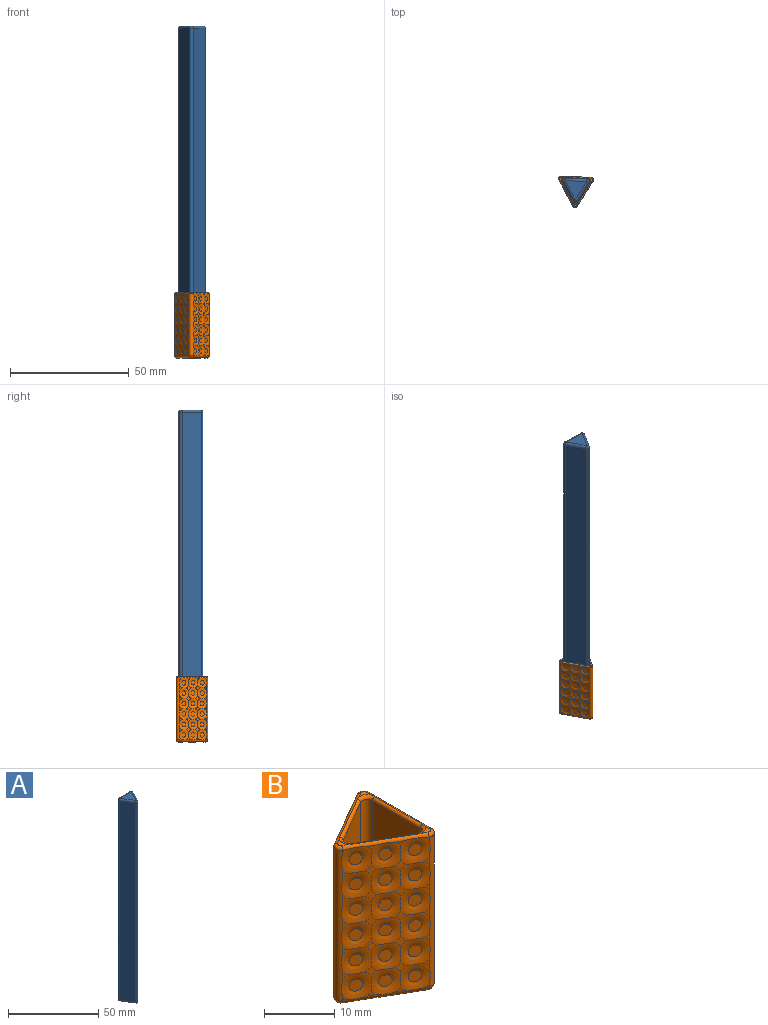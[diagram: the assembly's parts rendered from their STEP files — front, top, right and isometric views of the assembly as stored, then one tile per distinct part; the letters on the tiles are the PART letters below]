
ASSEMBLY  parts=2 mates=1
PART A: 20 faces, bbox 11.2x10.2x137.5 mm
  f0: plane 135.5x7.83mm, normal (-0.85,-0.53,0), area 1251.7mm2, adj f8,f13,f16,f19
  f1: plane 135.5x8.16mm, normal (0.88,-0.47,0), area 1251.7mm2, adj f6,f14,f15,f19
  f2: plane 135.5x9.23mm, normal (-0.04,1,0), area 1251.7mm2, adj f5,f6,f7,f8
  f3: plane 9.23x8.16mm, normal (0,0,1), area 37mm2, adj f5,f13,f14
  f4: plane 9.23x8.16mm, normal (0,0,-1), area 37mm2, adj f7,f15,f16
  f5: cylinder r=1mm len=9.27mm, axis (1,0.04,0), area 14.5mm2, adj f2,f3,f9,f10
  f6: cylinder r=1mm len=135.5mm, axis (0,0,-1), area 283.8mm2, adj f1,f2,f10,f11
  f7: cylinder r=1mm len=9.27mm, axis (-1,-0.04,0), area 14.5mm2, adj f2,f4,f11,f12
  f8: cylinder r=1mm len=135.5mm, axis (0,0,-1), area 283.8mm2, adj f0,f2,f9,f12
  f9: sphere r=1mm, area 2.1mm2, adj f5,f8,f13
  f10: sphere r=1mm, area 2.1mm2, adj f5,f6,f14
  f11: sphere r=1mm, area 2.1mm2, adj f6,f7,f15
  f12: sphere r=1mm, area 2.1mm2, adj f7,f8,f16
  f13: cylinder r=1mm len=8.36mm, axis (-0.53,0.85,0), area 14.5mm2, adj f0,f3,f9,f17
  f14: cylinder r=1mm len=8.63mm, axis (-0.47,-0.88,0), area 14.5mm2, adj f1,f3,f10,f17
  f15: cylinder r=1mm len=8.63mm, axis (0.47,0.88,0), area 14.5mm2, adj f1,f4,f11,f18
  f16: cylinder r=1mm len=8.36mm, axis (0.53,-0.85,0), area 14.5mm2, adj f0,f4,f12,f18
  f17: sphere r=1mm, area 2.1mm2, adj f13,f14,f19
  f18: sphere r=1mm, area 2.1mm2, adj f15,f16,f19
  f19: cylinder r=1mm len=135.5mm, axis (0,0,-1), area 283.8mm2, adj f0,f1,f17,f18
PART B: 243 faces, bbox 13.2x14.9x27.6 mm
  f0: plane 0.94x0.82mm, normal (0,0,-1), area 0.4mm2, adj f99,f105,f242
  f1: plane 0.94x0.82mm, normal (0,0,-1), area 0.4mm2, adj f99,f102,f240
  f2: plane 3.04x1.28mm, normal (0,0,-1), area 2.7mm2, adj f99,f240,f241,f242
  f3: plane 2.76x2.34mm, normal (0,0,-1), area 2.7mm2, adj f105,f239,f241,f242
  f4: plane 0.94x0.82mm, normal (0,0,-1), area 0.4mm2, adj f102,f105,f239
  f5: plane 0.4x0.35mm, normal (-0.5,-0.87,0), area 0.1mm2, adj f101,f102,f234
  f6: plane 0.4x0.35mm, normal (-0.5,-0.87,0), area 0.1mm2, adj f97,f102,f231
  f7: plane 1x0.65mm, normal (-0.5,-0.87,0), area 0.3mm2, adj f102,f231,f233
  f8: plane 1x0.65mm, normal (-0.5,-0.87,0), area 0.3mm2, adj f102,f233,f234
  f9: plane 1.2x0.6mm, normal (-0.5,-0.87,0), area 0.4mm2, adj f97,f228,f231
  f10: plane 1.7x1.5mm, normal (-0.5,-0.87,0), area 1.2mm2, adj f228,f230,f231,f233
  f11: plane 1.7x1.5mm, normal (-0.5,-0.87,0), area 1.2mm2, adj f230,f232,f233,f234
  f12: plane 1.2x0.6mm, normal (-0.5,-0.87,0), area 0.4mm2, adj f101,f232,f234
  f13: plane 1.7x1.5mm, normal (-0.5,-0.87,0), area 1.2mm2, adj f227,f229,f230,f232
  f14: plane 1.2x0.6mm, normal (-0.5,-0.87,0), area 0.4mm2, adj f101,f229,f232
  f15: plane 1.2x0.6mm, normal (-0.5,-0.87,0), area 0.4mm2, adj f97,f225,f228
  f16: plane 1.7x1.5mm, normal (-0.5,-0.87,0), area 1.2mm2, adj f225,f227,f228,f230
  f17: plane 1.2x0.6mm, normal (-0.5,-0.87,0), area 0.4mm2, adj f97,f222,f225
  f18: plane 1.7x1.5mm, normal (-0.5,-0.87,0), area 1.2mm2, adj f222,f224,f225,f227
  f19: plane 1.7x1.5mm, normal (-0.5,-0.87,0), area 1.2mm2, adj f224,f226,f227,f229
  f20: plane 1.2x0.6mm, normal (-0.5,-0.87,0), area 0.4mm2, adj f101,f226,f229
  f21: plane 1.2x0.6mm, normal (-0.5,-0.87,0), area 0.4mm2, adj f101,f223,f226
  f22: plane 1.7x1.5mm, normal (-0.5,-0.87,0), area 1.2mm2, adj f221,f223,f224,f226
  f23: plane 1.2x0.6mm, normal (-0.5,-0.87,0), area 0.4mm2, adj f97,f219,f222
  f24: plane 1.7x1.5mm, normal (-0.5,-0.87,0), area 1.2mm2, adj f219,f221,f222,f224
  f25: plane 0.4x0.35mm, normal (-0.5,-0.87,0), area 0.1mm2, adj f97,f123,f217
  f26: plane 1.2x0.6mm, normal (-0.5,-0.87,0), area 0.4mm2, adj f97,f217,f219
  f27: plane 1x0.65mm, normal (-0.5,-0.87,0), area 0.3mm2, adj f123,f217,f218
  f28: plane 1.7x1.5mm, normal (-0.5,-0.87,0), area 1.2mm2, adj f217,f218,f219,f221
  f29: plane 1.7x1.5mm, normal (-0.5,-0.87,0), area 1.2mm2, adj f218,f220,f221,f223
  f30: plane 1.2x0.6mm, normal (-0.5,-0.87,0), area 0.4mm2, adj f101,f220,f223
  f31: plane 0.4x0.35mm, normal (-0.5,-0.87,0), area 0.1mm2, adj f101,f123,f220
  f32: plane 0.69x0.6mm, normal (-0.5,0.87,0), area 0.2mm2, adj f101,f105,f198
  f33: plane 1.78x0.92mm, normal (-0.5,0.87,0), area 0.8mm2, adj f101,f197,f198
  f34: plane 1.78x0.92mm, normal (-0.5,0.87,0), area 0.8mm2, adj f101,f195,f197
  f35: plane 1.5x1.01mm, normal (-0.5,0.87,0), area 0.7mm2, adj f105,f196,f198
  f36: plane 2.41x2.14mm, normal (-0.5,0.87,0), area 2.2mm2, adj f194,f196,f197,f198
  f37: plane 1.5x1.01mm, normal (-0.5,0.87,0), area 0.7mm2, adj f105,f193,f196
  f38: plane 0.69x0.6mm, normal (-0.5,0.87,0), area 0.2mm2, adj f100,f105,f193
  f39: plane 2.41x2.14mm, normal (-0.5,0.87,0), area 2.2mm2, adj f190,f193,f194,f196
  f40: plane 1.78x0.92mm, normal (-0.5,0.87,0), area 0.8mm2, adj f100,f190,f193
  f41: plane 2.41x2.14mm, normal (-0.5,0.87,0), area 2.2mm2, adj f191,f194,f195,f197
  f42: plane 2.41x2.14mm, normal (-0.5,0.87,0), area 2.2mm2, adj f187,f190,f191,f194
  f43: plane 1.78x0.92mm, normal (-0.5,0.87,0), area 0.8mm2, adj f100,f187,f190
  f44: plane 1.78x0.92mm, normal (-0.5,0.87,0), area 0.8mm2, adj f101,f192,f195
  f45: plane 2.41x2.14mm, normal (-0.5,0.87,0), area 2.2mm2, adj f188,f191,f192,f195
  f46: plane 2.41x2.14mm, normal (-0.5,0.87,0), area 2.2mm2, adj f184,f187,f188,f191
  f47: plane 1.78x0.92mm, normal (-0.5,0.87,0), area 0.8mm2, adj f100,f184,f187
  f48: plane 1.78x0.92mm, normal (-0.5,0.87,0), area 0.8mm2, adj f101,f189,f192
  f49: plane 2.41x2.14mm, normal (-0.5,0.87,0), area 2.2mm2, adj f185,f188,f189,f192
  f50: plane 2.41x2.14mm, normal (-0.5,0.87,0), area 2.2mm2, adj f182,f184,f185,f188
  f51: plane 1.78x0.92mm, normal (-0.5,0.87,0), area 0.8mm2, adj f100,f182,f184
  f52: plane 0.69x0.6mm, normal (-0.5,0.87,0), area 0.2mm2, adj f101,f124,f186
  f53: plane 1.78x0.92mm, normal (-0.5,0.87,0), area 0.8mm2, adj f101,f186,f189
  f54: plane 1.5x1.01mm, normal (-0.5,0.87,0), area 0.7mm2, adj f124,f183,f186
  f55: plane 2.41x2.14mm, normal (-0.5,0.87,0), area 2.2mm2, adj f183,f185,f186,f189
  f56: plane 2.41x2.14mm, normal (-0.5,0.87,0), area 2.2mm2, adj f181,f182,f183,f185
  f57: plane 1.78x0.92mm, normal (-0.5,0.87,0), area 0.8mm2, adj f100,f181,f182
  f58: plane 0.69x0.6mm, normal (-0.5,0.87,0), area 0.2mm2, adj f100,f124,f181
  f59: plane 0.69x0.69mm, normal (1,0,0), area 0.2mm2, adj f97,f115,f162
  f60: plane 0.69x0.69mm, normal (1,0,0), area 0.2mm2, adj f100,f115,f158
  f61: plane 1.73x1.01mm, normal (1,0,0), area 0.7mm2, adj f115,f161,f162
  f62: plane 1.73x1.01mm, normal (1,0,0), area 0.7mm2, adj f115,f158,f161
  f63: plane 1.78x1.06mm, normal (1,0,0), area 0.8mm2, adj f100,f155,f158
  f64: plane 2.47x2.41mm, normal (1,0,0), area 2.2mm2, adj f155,f158,f159,f161
  f65: plane 1.78x1.06mm, normal (1,0,0), area 0.8mm2, adj f97,f160,f162
  f66: plane 2.47x2.41mm, normal (1,0,0), area 2.2mm2, adj f159,f160,f161,f162
  f67: plane 1.78x1.06mm, normal (1,0,0), area 0.8mm2, adj f97,f157,f160
  f68: plane 2.47x2.41mm, normal (1,0,0), area 2.2mm2, adj f156,f157,f159,f160
  f69: plane 2.47x2.41mm, normal (1,0,0), area 2.2mm2, adj f152,f155,f156,f159
  f70: plane 1.78x1.06mm, normal (1,0,0), area 0.8mm2, adj f100,f152,f155
  f71: plane 1.78x1.06mm, normal (1,0,0), area 0.8mm2, adj f100,f149,f152
  f72: plane 1.78x1.06mm, normal (1,0,0), area 0.8mm2, adj f100,f146,f149
  f73: plane 2.47x2.41mm, normal (1,0,0), area 2.2mm2, adj f149,f152,f153,f156
  f74: plane 2.47x2.41mm, normal (1,0,0), area 2.2mm2, adj f146,f149,f150,f153
  f75: plane 1.78x1.06mm, normal (1,0,0), area 0.8mm2, adj f97,f154,f157
  f76: plane 2.47x2.41mm, normal (1,0,0), area 2.2mm2, adj f153,f154,f156,f157
  f77: plane 1.78x1.06mm, normal (1,0,0), area 0.8mm2, adj f97,f151,f154
  f78: plane 2.47x2.41mm, normal (1,0,0), area 2.2mm2, adj f150,f151,f153,f154
  f79: plane 0.69x0.69mm, normal (1,0,0), area 0.2mm2, adj f97,f99,f148
  f80: plane 1.78x1.06mm, normal (1,0,0), area 0.8mm2, adj f97,f148,f151
  f81: plane 1.73x1.01mm, normal (1,0,0), area 0.7mm2, adj f99,f147,f148
  f82: plane 2.47x2.41mm, normal (1,0,0), area 2.2mm2, adj f147,f148,f150,f151
  f83: plane 2.47x2.41mm, normal (1,0,0), area 2.2mm2, adj f145,f146,f147,f150
  f84: plane 1.78x1.06mm, normal (1,0,0), area 0.8mm2, adj f100,f145,f146
  f85: plane 0.69x0.69mm, normal (1,0,0), area 0.2mm2, adj f99,f100,f145
  f86: plane 1.89x1.13mm, normal (0,0,1), area 0.9mm2, adj f119,f123,f124,f126
  f87: plane 1.63x1.52mm, normal (0,0,1), area 0.9mm2, adj f115,f117,f118,f123
  f88: plane 1x0.65mm, normal (-0.5,-0.87,0), area 0.3mm2, adj f123,f218,f220
  f89: plane 1.73x1.01mm, normal (1,0,0), area 0.7mm2, adj f99,f145,f147
  f90: plane 23.5x9.58mm, normal (-1,0,0), area 225.2mm2, adj f108,f112,f114,f116
  f91: plane 23.5x8.3mm, normal (0.5,0.87,0), area 225.2mm2, adj f106,f111,f114,f122
  f92: plane 23.5x8.3mm, normal (0.5,-0.87,0), area 225.2mm2, adj f106,f107,f108,f125
  f93: plane 1.5x1.01mm, normal (-0.5,0.87,0), area 0.7mm2, adj f124,f181,f183
  f94: plane 1.63x1.52mm, normal (0,0,1), area 0.9mm2, adj f115,f120,f121,f124
  f95: plane 9.58x8.3mm, normal (0,0,1), area 39.8mm2, adj f107,f111,f112
  f96: plane 2.76x2.34mm, normal (0,0,-1), area 2.7mm2, adj f102,f239,f240,f241
  f97: cylinder r=1mm len=26mm, axis (0,0,-1), area 50.9mm2, adj f6,f9,f15,f17,f23,f25,f26,f59
  f98: sphere r=1mm, area 2.1mm2, adj f97,f99,f102
  f99: cylinder r=1mm len=12.7mm, axis (0,-1,0), area 17.9mm2, adj f0,f1,f2,f79,f81,f85,f89,f98
  f100: cylinder r=1mm len=26mm, axis (0,0,-1), area 51.7mm2, adj f38,f40,f43,f47,f51,f57,f58,f60
  f101: cylinder r=1mm len=26mm, axis (0,0,-1), area 50.9mm2, adj f5,f12,f14,f20,f21,f30,f31,f32
  f102: cylinder r=1mm len=11.5mm, axis (-0.87,0.5,0), area 17.4mm2, adj f1,f4,f5,f6,f7,f8,f96,f98
  f103: sphere r=1mm, area 2.1mm2, adj f99,f100,f105
  f104: sphere r=1mm, area 2.1mm2, adj f101,f102,f105
  f105: cylinder r=1mm len=11.5mm, axis (0.87,0.5,0), area 17.9mm2, adj f0,f3,f4,f32,f35,f37,f38,f103
  f106: cylinder r=1mm len=23.5mm, axis (0,0,1), area 49.2mm2, adj f91,f92,f109,f126
  f107: cylinder r=1mm len=8.8mm, axis (-0.87,-0.5,0), area 15.1mm2, adj f92,f95,f109,f110
  f108: cylinder r=1mm len=23.5mm, axis (0,0,1), area 49.2mm2, adj f90,f92,f110,f121
  f109: sphere r=1mm, area 2.1mm2, adj f106,f107,f111
  f110: sphere r=1mm, area 2.1mm2, adj f107,f108,f112
  f111: cylinder r=1mm len=8.8mm, axis (0.87,-0.5,0), area 15.1mm2, adj f91,f95,f109,f113
  f112: cylinder r=1mm len=9.58mm, axis (0,1,0), area 15.1mm2, adj f90,f95,f110,f113
  f113: sphere r=1mm, area 2.1mm2, adj f111,f112,f114
  f114: cylinder r=1mm len=23.5mm, axis (0,0,1), area 49.2mm2, adj f90,f91,f113,f117
  f115: cylinder r=0.5mm len=12.7mm, axis (0,-1,0), area 8.9mm2, adj f59,f60,f61,f62,f87,f94,f116,f117
  f116: cylinder r=0.5mm len=9.58mm, axis (0,1,0), area 7mm2, adj f90,f115,f117,f121
  f117: torus R=1.5mm, axis (0,0,1), area 1.9mm2, adj f87,f114,f115,f116,f122,f123
  f118: torus R=0.5mm, axis (0,0,1), area 1.3mm2, adj f87,f97,f115,f123
  f119: torus R=0.5mm, axis (0,0,1), area 1.3mm2, adj f86,f101,f123,f124
  f120: torus R=0.5mm, axis (0,0,1), area 1.3mm2, adj f94,f100,f115,f124
  f121: torus R=1.5mm, axis (0,0,1), area 1.9mm2, adj f94,f108,f115,f116,f124,f125
  f122: cylinder r=0.5mm len=8.53mm, axis (0.87,-0.5,0), area 7mm2, adj f91,f117,f123,f126
  f123: cylinder r=0.5mm len=11.25mm, axis (-0.87,0.5,0), area 8.6mm2, adj f25,f27,f31,f86,f87,f88,f117,f118
  f124: cylinder r=0.5mm len=11.25mm, axis (0.87,0.5,0), area 8.9mm2, adj f52,f54,f58,f86,f93,f94,f119,f120
  f125: cylinder r=0.5mm len=8.53mm, axis (-0.87,-0.5,0), area 7mm2, adj f92,f121,f124,f126
  f126: torus R=1.5mm, axis (0,0,1), area 1.9mm2, adj f86,f106,f122,f123,f124,f125
  f127: plane 2x2mm, normal (1,0,0), area 3.1mm2, adj f145
  f128: plane 2x2mm, normal (1,0,0), area 3.1mm2, adj f158
  f129: plane 2x2mm, normal (1,0,0), area 3.1mm2, adj f157
  f130: plane 2x2mm, normal (1,0,0), area 3.1mm2, adj f156
  f131: plane 2x2mm, normal (1,0,0), area 3.1mm2, adj f152
  f132: plane 2x2mm, normal (1,0,0), area 3.1mm2, adj f155
  f133: plane 2x2mm, normal (1,0,0), area 3.1mm2, adj f159
  f134: plane 2x2mm, normal (1,0,0), area 3.1mm2, adj f160
  f135: plane 2x2mm, normal (1,0,0), area 3.1mm2, adj f162
  f136: plane 2x2mm, normal (1,0,0), area 3.1mm2, adj f161
  f137: plane 2x2mm, normal (1,0,0), area 3.1mm2, adj f147
  f138: plane 2x2mm, normal (1,0,0), area 3.1mm2, adj f148
  f139: plane 2x2mm, normal (1,0,0), area 3.1mm2, adj f151
  f140: plane 2x2mm, normal (1,0,0), area 3.1mm2, adj f150
  f141: plane 2x2mm, normal (1,0,0), area 3.1mm2, adj f146
  f142: plane 2x2mm, normal (1,0,0), area 3.1mm2, adj f149
  f143: plane 2x2mm, normal (1,0,0), area 3.1mm2, adj f153
  f144: plane 2x2mm, normal (1,0,0), area 3.1mm2, adj f154
  f145: torus R=2.39mm, axis (-1,0,0), area 14.1mm2, adj f83,f84,f85,f89,f99,f100,f127,f146
  f146: torus R=2.39mm, axis (-1,0,0), area 14.6mm2, adj f72,f74,f83,f84,f100,f141,f145,f149
  f147: torus R=2.39mm, axis (-1,0,0), area 14.6mm2, adj f81,f82,f83,f89,f99,f137,f145,f148
  f148: torus R=2.39mm, axis (-1,0,0), area 14.1mm2, adj f79,f80,f81,f82,f97,f99,f138,f147
  f149: torus R=2.39mm, axis (-1,0,0), area 14.6mm2, adj f71,f72,f73,f74,f100,f142,f146,f152
  f150: torus R=2.39mm, axis (-1,0,0), area 15.1mm2, adj f74,f78,f82,f83,f140,f146,f147,f151
  f151: torus R=2.39mm, axis (-1,0,0), area 14.6mm2, adj f77,f78,f80,f82,f97,f139,f148,f150
  f152: torus R=2.39mm, axis (-1,0,0), area 14.6mm2, adj f69,f70,f71,f73,f100,f131,f149,f155
  f153: torus R=2.39mm, axis (-1,0,0), area 15.1mm2, adj f73,f74,f76,f78,f143,f149,f150,f154
  f154: torus R=2.39mm, axis (-1,0,0), area 14.6mm2, adj f75,f76,f77,f78,f97,f144,f151,f153
  f155: torus R=2.39mm, axis (-1,0,0), area 14.6mm2, adj f63,f64,f69,f70,f100,f132,f152,f158
  f156: torus R=2.39mm, axis (-1,0,0), area 15.1mm2, adj f68,f69,f73,f76,f130,f152,f153,f157
  f157: torus R=2.39mm, axis (-1,0,0), area 14.6mm2, adj f67,f68,f75,f76,f97,f129,f154,f156
  f158: torus R=2.39mm, axis (-1,0,0), area 14.1mm2, adj f60,f62,f63,f64,f100,f115,f128,f155
  f159: torus R=2.39mm, axis (-1,0,0), area 15.1mm2, adj f64,f66,f68,f69,f133,f155,f156,f160
  f160: torus R=2.39mm, axis (-1,0,0), area 14.6mm2, adj f65,f66,f67,f68,f97,f134,f157,f159
  f161: torus R=2.39mm, axis (-1,0,0), area 14.6mm2, adj f61,f62,f64,f66,f115,f136,f158,f159
  f162: torus R=2.39mm, axis (-1,0,0), area 14.1mm2, adj f59,f61,f65,f66,f97,f115,f135,f160
  f163: plane 2x1.73mm, normal (-0.5,0.87,0), area 3.1mm2, adj f181
  f164: plane 2x1.73mm, normal (-0.5,0.87,0), area 3.1mm2, adj f193
  f165: plane 2x1.73mm, normal (-0.5,0.87,0), area 3.1mm2, adj f195
  f166: plane 2x1.73mm, normal (-0.5,0.87,0), area 3.1mm2, adj f191
  f167: plane 2x1.73mm, normal (-0.5,0.87,0), area 3.1mm2, adj f187
  f168: plane 2x1.73mm, normal (-0.5,0.87,0), area 3.1mm2, adj f190
  f169: plane 2x1.73mm, normal (-0.5,0.87,0), area 3.1mm2, adj f194
  f170: plane 2x1.73mm, normal (-0.5,0.87,0), area 3.1mm2, adj f197
  f171: plane 2x1.73mm, normal (-0.5,0.87,0), area 3.1mm2, adj f198
  f172: plane 2x1.73mm, normal (-0.5,0.87,0), area 3.1mm2, adj f196
  f173: plane 2x1.73mm, normal (-0.5,0.87,0), area 3.1mm2, adj f183
  f174: plane 2x1.73mm, normal (-0.5,0.87,0), area 3.1mm2, adj f186
  f175: plane 2x1.73mm, normal (-0.5,0.87,0), area 3.1mm2, adj f189
  f176: plane 2x1.73mm, normal (-0.5,0.87,0), area 3.1mm2, adj f185
  f177: plane 2x1.73mm, normal (-0.5,0.87,0), area 3.1mm2, adj f182
  f178: plane 2x1.73mm, normal (-0.5,0.87,0), area 3.1mm2, adj f184
  f179: plane 2x1.73mm, normal (-0.5,0.87,0), area 3.1mm2, adj f188
  f180: plane 2x1.73mm, normal (-0.5,0.87,0), area 3.1mm2, adj f192
  f181: torus R=2.39mm, axis (0.5,-0.87,0), area 14.1mm2, adj f56,f57,f58,f93,f100,f124,f163,f182
  f182: torus R=2.39mm, axis (0.5,-0.87,0), area 14.6mm2, adj f50,f51,f56,f57,f100,f177,f181,f184
  f183: torus R=2.39mm, axis (0.5,-0.87,0), area 14.6mm2, adj f54,f55,f56,f93,f124,f173,f181,f185
  f184: torus R=2.39mm, axis (0.5,-0.87,0), area 14.6mm2, adj f46,f47,f50,f51,f100,f178,f182,f187
  f185: torus R=2.39mm, axis (0.5,-0.87,0), area 15.1mm2, adj f49,f50,f55,f56,f176,f182,f183,f188
  f186: torus R=2.39mm, axis (0.5,-0.87,0), area 14.1mm2, adj f52,f53,f54,f55,f101,f124,f174,f183
  f187: torus R=2.39mm, axis (0.5,-0.87,0), area 14.6mm2, adj f42,f43,f46,f47,f100,f167,f184,f190
  f188: torus R=2.39mm, axis (0.5,-0.87,0), area 15.1mm2, adj f45,f46,f49,f50,f179,f184,f185,f191
  f189: torus R=2.39mm, axis (0.5,-0.87,0), area 14.6mm2, adj f48,f49,f53,f55,f101,f175,f185,f186
  f190: torus R=2.39mm, axis (0.5,-0.87,0), area 14.6mm2, adj f39,f40,f42,f43,f100,f168,f187,f193
  f191: torus R=2.39mm, axis (0.5,-0.87,0), area 15.1mm2, adj f41,f42,f45,f46,f166,f187,f188,f194
  f192: torus R=2.39mm, axis (0.5,-0.87,0), area 14.6mm2, adj f44,f45,f48,f49,f101,f180,f188,f189
  f193: torus R=2.39mm, axis (0.5,-0.87,0), area 14.1mm2, adj f37,f38,f39,f40,f100,f105,f164,f190
  f194: torus R=2.39mm, axis (0.5,-0.87,0), area 15.1mm2, adj f36,f39,f41,f42,f169,f190,f191,f196
  f195: torus R=2.39mm, axis (0.5,-0.87,0), area 14.6mm2, adj f34,f41,f44,f45,f101,f165,f191,f192
  f196: torus R=2.39mm, axis (0.5,-0.87,0), area 14.6mm2, adj f35,f36,f37,f39,f105,f172,f193,f194
  f197: torus R=2.39mm, axis (0.5,-0.87,0), area 14.6mm2, adj f33,f34,f36,f41,f101,f170,f194,f195
  f198: torus R=2.39mm, axis (0.5,-0.87,0), area 14.1mm2, adj f32,f33,f35,f36,f101,f105,f171,f196
  f199: plane 2x1.73mm, normal (-0.5,-0.87,0), area 3.1mm2, adj f234
  f200: plane 2x1.73mm, normal (-0.5,-0.87,0), area 3.1mm2, adj f228
  f201: plane 2x1.73mm, normal (-0.5,-0.87,0), area 3.1mm2, adj f217
  f202: plane 2x1.73mm, normal (-0.5,-0.87,0), area 3.1mm2, adj f223
  f203: plane 2x1.73mm, normal (-0.5,-0.87,0), area 3.1mm2, adj f221
  f204: plane 2x1.73mm, normal (-0.5,-0.87,0), area 3.1mm2, adj f219
  f205: plane 2x1.73mm, normal (-0.5,-0.87,0), area 3.1mm2, adj f218
  f206: plane 2x1.73mm, normal (-0.5,-0.87,0), area 3.1mm2, adj f220
  f207: plane 2x1.73mm, normal (-0.5,-0.87,0), area 3.1mm2, adj f231
  f208: plane 2x1.73mm, normal (-0.5,-0.87,0), area 3.1mm2, adj f233
  f209: plane 2x1.73mm, normal (-0.5,-0.87,0), area 3.1mm2, adj f230
  f210: plane 2x1.73mm, normal (-0.5,-0.87,0), area 3.1mm2, adj f232
  f211: plane 2x1.73mm, normal (-0.5,-0.87,0), area 3.1mm2, adj f224
  f212: plane 2x1.73mm, normal (-0.5,-0.87,0), area 3.1mm2, adj f225
  f213: plane 2x1.73mm, normal (-0.5,-0.87,0), area 3.1mm2, adj f227
  f214: plane 2x1.73mm, normal (-0.5,-0.87,0), area 3.1mm2, adj f229
  f215: plane 2x1.73mm, normal (-0.5,-0.87,0), area 3.1mm2, adj f226
  f216: plane 2x1.73mm, normal (-0.5,-0.87,0), area 3.1mm2, adj f222
  f217: torus R=2.56mm, axis (0.5,0.87,0), area 14.5mm2, adj f25,f26,f27,f28,f97,f123,f201,f218
  f218: torus R=2.56mm, axis (0.5,0.87,0), area 14.7mm2, adj f27,f28,f29,f88,f123,f205,f217,f220
  f219: torus R=2.56mm, axis (0.5,0.87,0), area 14.8mm2, adj f23,f24,f26,f28,f97,f204,f217,f221
  f220: torus R=2.56mm, axis (0.5,0.87,0), area 14.5mm2, adj f29,f30,f31,f88,f101,f123,f206,f218
  f221: torus R=2.56mm, axis (0.5,0.87,0), area 15mm2, adj f22,f24,f28,f29,f203,f218,f219,f223
  f222: torus R=2.56mm, axis (0.5,0.87,0), area 14.8mm2, adj f17,f18,f23,f24,f97,f216,f219,f224
  f223: torus R=2.56mm, axis (0.5,0.87,0), area 14.8mm2, adj f21,f22,f29,f30,f101,f202,f220,f221
  f224: torus R=2.56mm, axis (0.5,0.87,0), area 15mm2, adj f18,f19,f22,f24,f211,f221,f222,f226
  f225: torus R=2.56mm, axis (0.5,0.87,0), area 14.8mm2, adj f15,f16,f17,f18,f97,f212,f222,f227
  f226: torus R=2.56mm, axis (0.5,0.87,0), area 14.8mm2, adj f19,f20,f21,f22,f101,f215,f223,f224
  f227: torus R=2.56mm, axis (0.5,0.87,0), area 15mm2, adj f13,f16,f18,f19,f213,f224,f225,f229
  f228: torus R=2.56mm, axis (0.5,0.87,0), area 14.8mm2, adj f9,f10,f15,f16,f97,f200,f225,f230
  f229: torus R=2.56mm, axis (0.5,0.87,0), area 14.8mm2, adj f13,f14,f19,f20,f101,f214,f226,f227
  f230: torus R=2.56mm, axis (0.5,0.87,0), area 15mm2, adj f10,f11,f13,f16,f209,f227,f228,f232
  f231: torus R=2.56mm, axis (0.5,0.87,0), area 14.6mm2, adj f6,f7,f9,f10,f97,f102,f207,f228
  f232: torus R=2.56mm, axis (0.5,0.87,0), area 14.8mm2, adj f11,f12,f13,f14,f101,f210,f229,f230
  f233: torus R=2.56mm, axis (0.5,0.87,0), area 14.8mm2, adj f7,f8,f10,f11,f102,f208,f230,f231
  f234: torus R=2.56mm, axis (0.5,0.87,0), area 14.6mm2, adj f5,f8,f11,f12,f101,f102,f199,f232
  f235: plane 2x2mm, normal (0,0,-1), area 3.1mm2, adj f241
  f236: plane 2x2mm, normal (0,0,-1), area 3.1mm2, adj f240
  f237: plane 2x2mm, normal (0,0,-1), area 3.1mm2, adj f242
  f238: plane 2x2mm, normal (0,0,-1), area 3.1mm2, adj f239
  f239: torus R=2.56mm, axis (0,0,-1), area 13.4mm2, adj f3,f4,f96,f102,f105,f238,f241
  f240: torus R=2.56mm, axis (0,0,-1), area 13mm2, adj f1,f2,f96,f99,f102,f236,f241
  f241: torus R=2.56mm, axis (0,0,-1), area 14.3mm2, adj f2,f3,f96,f235,f239,f240,f242
  f242: torus R=2.56mm, axis (0,0,-1), area 13mm2, adj f0,f2,f3,f99,f105,f237,f241
PLACE A rot(axis=(0,0,-1),4deg) t=(-23.71,-43,-94.93)mm
PLACE B rot(axis=(0,0,1),88deg) t=(-43.9,-1.63,-94.93)mm
MATE cylindrical A.f4 <-> B.f241  axis (0,0,-1) through (-23.71,-43,-94.93)mm
